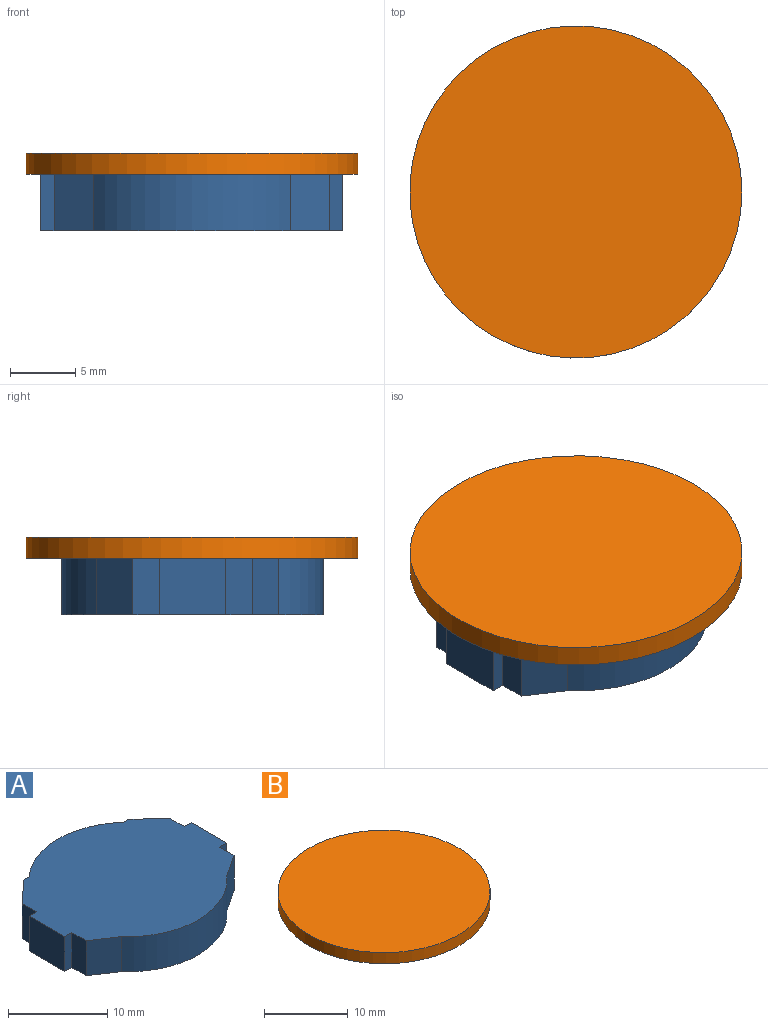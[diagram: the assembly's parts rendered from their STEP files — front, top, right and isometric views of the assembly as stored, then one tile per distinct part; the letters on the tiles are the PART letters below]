
ASSEMBLY  parts=2 mates=1
PART A: 20 faces, bbox 23.1x20x4.3 mm
  f0: cylinder r=9.99mm len=13.51mm, axis (0,0,1), area 64.1mm2, adj f1,f17,f18,f19
  f1: plane 4.32x0.74mm, normal (0,1,0), area 3.2mm2, adj f0,f2,f18,f19
  f2: plane 4.32x3.05mm, normal (-0.68,0.74,0), area 17.9mm2, adj f1,f3,f18,f19
  f3: plane 4.32x2.03mm, normal (-1,0,0), area 8.8mm2, adj f2,f4,f18,f19
  f4: plane 4.32x1.02mm, normal (0,1,0), area 4.4mm2, adj f3,f5,f18,f19
  f5: plane 5.08x4.32mm, normal (-1,0,0), area 21.9mm2, adj f4,f6,f18,f19
  f6: plane 4.32x1.02mm, normal (0,-1,0), area 4.4mm2, adj f5,f7,f18,f19
  f7: plane 4.32x2.03mm, normal (-1,0,0), area 8.8mm2, adj f6,f8,f18,f19
  f8: plane 4.32x3.03mm, normal (-0.55,-0.83,0), area 15.7mm2, adj f7,f9,f18,f19
  f9: cylinder r=9.99mm len=15.03mm, axis (0,0,1), area 73.5mm2, adj f8,f10,f18,f19
  f10: plane 4.32x3.03mm, normal (0.55,-0.83,0), area 15.7mm2, adj f9,f11,f18,f19
  f11: plane 4.32x2.03mm, normal (1,0,0), area 8.8mm2, adj f10,f12,f18,f19
  f12: plane 4.32x1.02mm, normal (0,-1,0), area 4.4mm2, adj f11,f13,f18,f19
  f13: plane 5.08x4.32mm, normal (1,0,0), area 21.9mm2, adj f12,f14,f18,f19
  f14: plane 4.32x1.02mm, normal (0,1,0), area 4.4mm2, adj f13,f15,f18,f19
  f15: plane 4.32x2.03mm, normal (1,0,0), area 8.8mm2, adj f14,f16,f18,f19
  f16: plane 4.32x3.05mm, normal (0.68,0.74,0), area 17.9mm2, adj f15,f17,f18,f19
  f17: plane 4.32x0.74mm, normal (0,1,0), area 3.2mm2, adj f0,f16,f18,f19
  f18: plane 23.11x19.99mm, normal (0,0,-1), area 349.8mm2, adj f0,f1,f2,f3,f4,f5,f6,f7
  f19: plane 23.11x19.99mm, normal (0,0,1), area 349.8mm2, adj f0,f1,f2,f3,f4,f5,f6,f7
PART B: 3 faces, bbox 25.4x25.4x1.6 mm
  f0: cylinder r=12.7mm len=25.4mm, axis (0,0,-1), area 129.7mm2, adj f1,f2
  f1: plane 25.4x25.4mm, normal (0,0,1), area 506.7mm2, adj f0
  f2: plane 25.4x25.4mm, normal (0,0,-1), area 506.7mm2, adj f0
PLACE A t=(0,-0.05,0)mm
PLACE B at identity
MATE fastened A.f19 <-> B.f0  axis (0,0,1) through (0,0,0)mm
